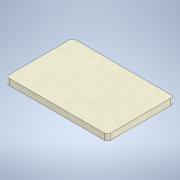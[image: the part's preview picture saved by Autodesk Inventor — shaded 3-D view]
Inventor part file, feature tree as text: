
AUTODESK INVENTOR PART (.ipt)
format: ipt  version: 2021 (Build 250183000, 183)  size: 111,104 bytes
history: native  units: mm
features: extrude x1, sketch x1
ambient origin geometry x8: Origin, YZ Plane, XZ Plane, XY Plane, X Axis, Y Axis, Z Axis, Center Point
bodies: Solid1 (feature_tree)
feature tree (2):
  extrude  "Extrusion1"  Depth=42.0mm
  sketch  "Sketch1"  dims[d0=64.0mm d1=42.0mm d2=2.0mm d3=3.9mm d4=0.0mm]
